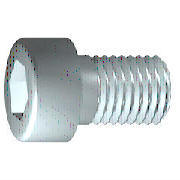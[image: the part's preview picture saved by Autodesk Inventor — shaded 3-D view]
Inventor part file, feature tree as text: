
AUTODESK INVENTOR PART (.ipt)
format: ipt  version: 2020 (Build 240168000, 168)  size: 193,024 bytes
history: native  units: mm (DEFAULTED — no unit token found)
features: sketch x2, other x1, extrude x1, plane x1, fillet x1
ambient origin geometry x7: Origin, YZ Plane, XY Plane, X Axis, Y Axis, Z Axis, Center Point
bodies: Solid1 (feature_tree)
feature tree (6):
  other  "Bryła"
  extrude  "Szczelina"  Depth=22.6mm
  plane  "Work Plane1"
  fillet  "Fillet2"  Radius=0.49086mm
  sketch  "Szkic1"
  sketch  "Szkic2"
